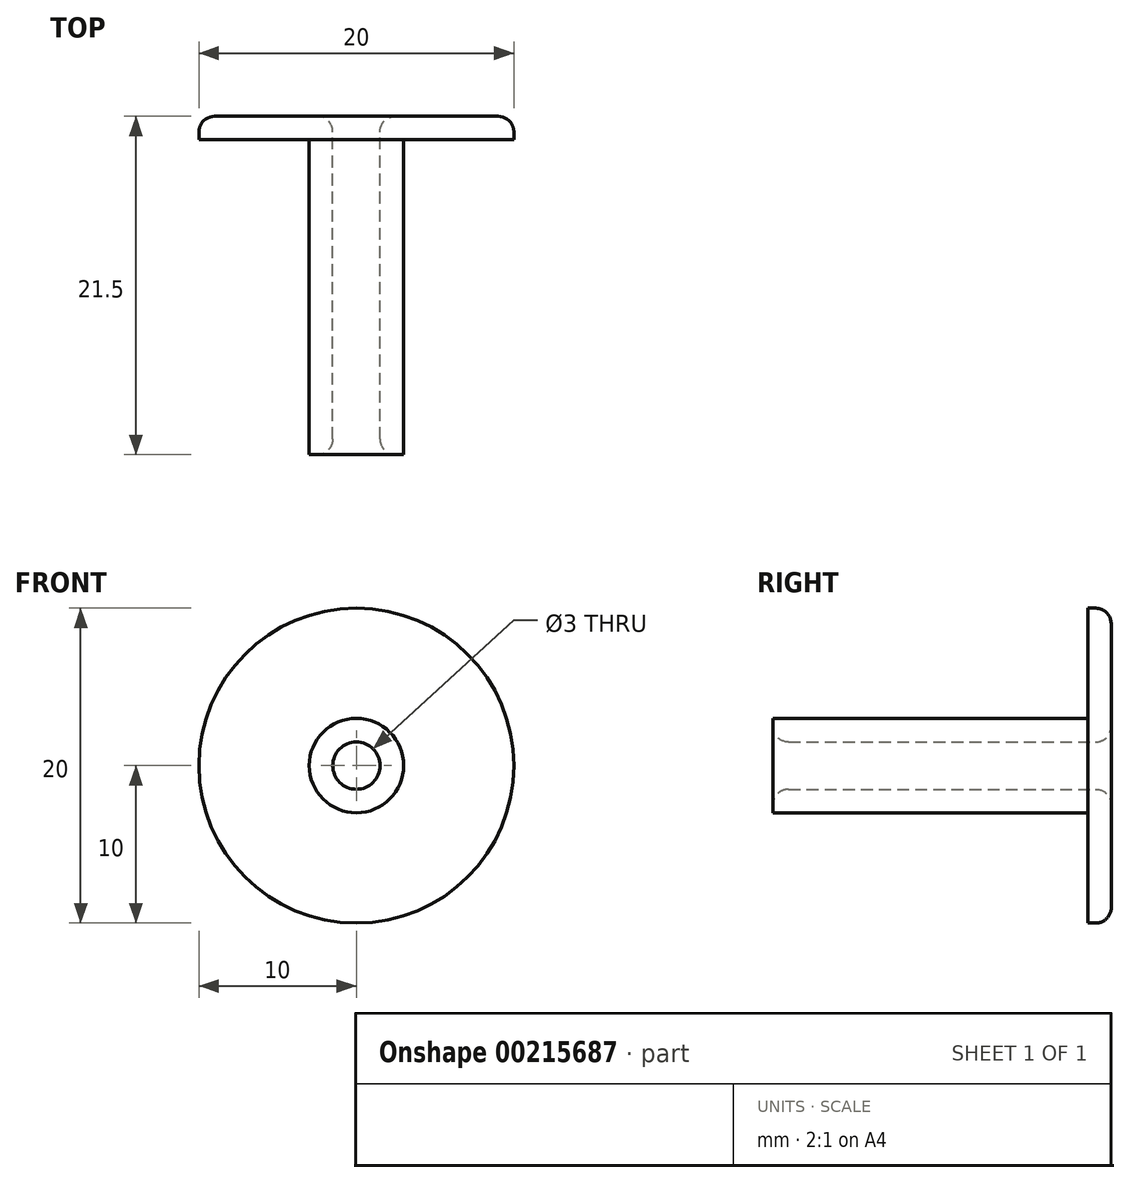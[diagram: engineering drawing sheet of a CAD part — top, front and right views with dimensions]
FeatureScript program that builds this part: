
annotation { "Feature Type Name" : "Feature", "Feature Type Description" : "" }
export const myFeature = defineFeature(function(context is Context, id is Id, definition is map)
    precondition{}
    {
        {
            var Q0;
            Q0=qCreatedBy(makeId("Top.planeOp"),FACE);
            var sketch = newSketch(context, id + "F0", { "sketchPlane" : qUnion([Q0])});
            skLineSegment(sketch, "E0", {"start": v(0, 21.16) * mm, "end": v(0, -26.64) * mm, "construction": true});
            skLineSegment(sketch, "E1", {"start": v(-10, 0) * mm, "end": v(-1.5, 0) * mm});
            skLineSegment(sketch, "E2", {"start": v(-1.5, 0) * mm, "end": v(-1.5, -21.5) * mm});
            skLineSegment(sketch, "E3", {"start": v(-1.5, -21.5) * mm, "end": v(-3, -21.5) * mm});
            skLineSegment(sketch, "E4", {"start": v(-3, -21.5) * mm, "end": v(-3, -1.5) * mm});
            skLineSegment(sketch, "E5", {"start": v(-3, -1.5) * mm, "end": v(-10, -1.5) * mm});
            skLineSegment(sketch, "E6", {"start": v(-10, -1.5) * mm, "end": v(-10, 0) * mm});
            skSolve(sketch);
        }
        {
            var Q0;
            Q0 = qSketchRegion(id + "F0", true);
            var Q1;
            Q1=sQuery(id+"F0.wireOp",EDGE,"E0");
            revolve(context, id + "F1", {"entities" : qUnion([Q0]), "axis" : qUnion([Q1]), "revolveType" : RevolveType.FULL});
        }
        {
            var Q0;
            Q0=makeQuery(id+"F1.opRevolve","SWEPT_EDGE",EDGE,{"disambiguationData":[OSD([sQuery(id+"F0.wireOp",EDGE,"E1"),sQuery(id+"F0.wireOp",EDGE,"E2")])]});
            var Q1;
            Q1=makeQuery(id+"F1.opRevolve","SWEPT_EDGE",EDGE,{"disambiguationData":[OSD([sQuery(id+"F0.wireOp",EDGE,"E1"),sQuery(id+"F0.wireOp",EDGE,"E6")])]});
            var Q2;
            Q2=makeQuery(id+"F1.opRevolve","SWEPT_EDGE",EDGE,{"disambiguationData":[OSD([sQuery(id+"F0.wireOp",EDGE,"E2"),sQuery(id+"F0.wireOp",EDGE,"E3")])]});
            fillet(context, id + "F2", {"entities" : qUnion([Q0, Q1, Q2]), "radius" : 1 * mm, "tangentPropagation" : true, "allowEdgeOverflow" : false});
        }
    });
